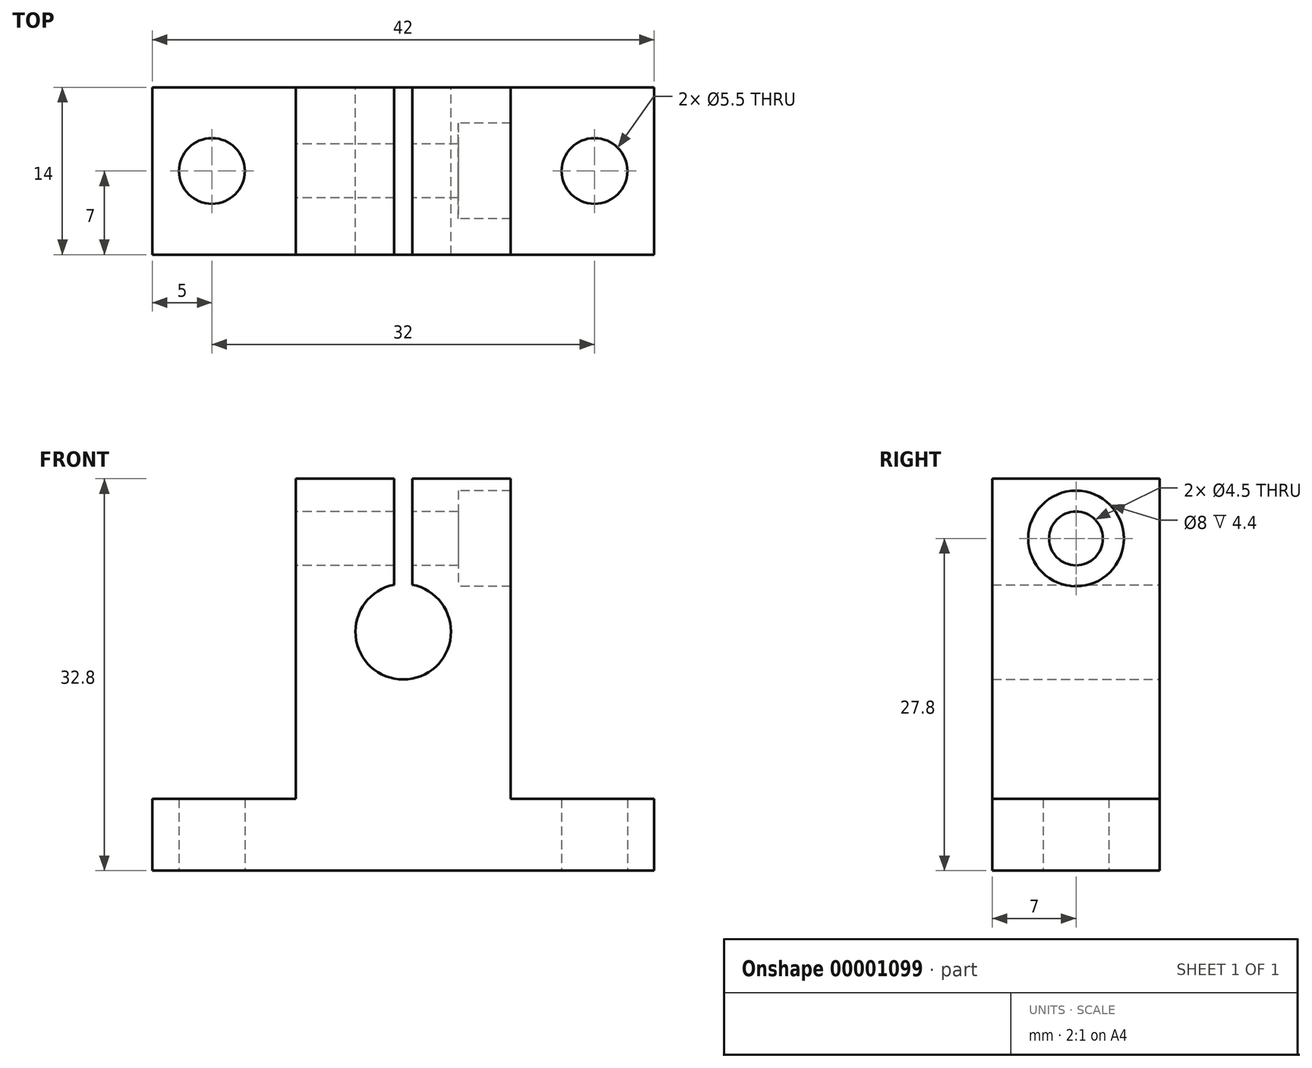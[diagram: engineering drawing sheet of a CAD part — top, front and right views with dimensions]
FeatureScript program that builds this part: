
annotation { "Feature Type Name" : "Feature", "Feature Type Description" : "" }
export const myFeature = defineFeature(function(context is Context, id is Id, definition is map)
    precondition{}
    {
        {
            var Q0;
            Q0=qCreatedBy(makeId("Front.planeOp"),FACE);
            var sketch = newSketch(context, id + "F0", { "sketchPlane" : qUnion([Q0])});
            skLineSegment(sketch, "E0", {"start": v(-21, 6) * mm, "end": v(-9, 6) * mm});
            skLineSegment(sketch, "E1", {"start": v(-9, 6) * mm, "end": v(-9, 32.8) * mm});
            skLineSegment(sketch, "E2", {"start": v(-9, 32.8) * mm, "end": v(-0.75, 32.8) * mm});
            skArc(sketch, "E3", {"start": v(-0.75, 23.93) * mm, "mid": v(0, 16) * mm, "end": v(0.75, 23.93) * mm});
            skLineSegment(sketch, "E4", {"start": v(0, 16) * mm, "end": v(0, 0) * mm, "construction": true});
            skLineSegment(sketch, "E5", {"start": v(21, 0) * mm, "end": v(-21, 0) * mm});
            skLineSegment(sketch, "E6", {"start": v(-21, 0) * mm, "end": v(-21, 6) * mm});
            skLineSegment(sketch, "E7", {"start": v(-0.75, 23.93) * mm, "end": v(-0.75, 32.8) * mm});
            skLineSegment(sketch, "E8.MirrorCS", {"start": v(21, 0) * mm, "end": v(21, 6) * mm});
            skLineSegment(sketch, "E9.MirrorCS", {"start": v(21, 6) * mm, "end": v(9, 6) * mm});
            skLineSegment(sketch, "E10.MirrorCS", {"start": v(9, 6) * mm, "end": v(9, 32.8) * mm});
            skLineSegment(sketch, "E11.MirrorCS", {"start": v(9, 32.8) * mm, "end": v(0.75, 32.8) * mm});
            skLineSegment(sketch, "E12.MirrorCS", {"start": v(0.75, 23.93) * mm, "end": v(0.75, 32.8) * mm});
            skSolve(sketch);
        }
        {
            var Q0;
            Q0=makeQuery(id+"F0.imprint","IMPRINT",FACE,{"disambiguationData":[TD([[makeQuery(id+"F0.imprint","IMPRINT",EDGE,{"derivedFrom":sQuery(id+"F0.wireOp",EDGE,"E0")}),-1.0]])]});
            extrude(context, id + "F1", {"entities" : qUnion([Q0]), "depth" : 14 * mm, "symmetric" : true});
        }
        {
            var Q0;
            Q0=makeQuery(id+"F1.opExtrude","SWEPT_FACE",FACE,{"disambiguationData":[OSD([sQuery(id+"F0.wireOp",EDGE,"E0")])]});
            var sketch = newSketch(context, id + "F2", { "sketchPlane" : qUnion([Q0])});
            skLineSegment(sketch, "E13.bottom", {"start": v(-16, 7) * mm, "end": v(16, 7) * mm, "construction": true});
            skLineSegment(sketch, "E13.top", {"start": v(-16, -7) * mm, "end": v(16, -7) * mm, "construction": true});
            skLineSegment(sketch, "E13.left", {"start": v(-16, 7) * mm, "end": v(-16, -7) * mm, "construction": true});
            skLineSegment(sketch, "E13.right", {"start": v(16, 7) * mm, "end": v(16, -7) * mm, "construction": true});
            skLineSegment(sketch, "E14", {"start": v(-16, 0) * mm, "end": v(16, 0) * mm, "construction": true});
            skSolve(sketch);
        }
        {
            var Q0;
            Q0=sQuery(id+"F2.wireOp",VERTEX,"E14.start");
            var Q1;
            Q1=sQuery(id+"F2.wireOp",VERTEX,"E14.end");
            var Q2;
            Q2=makeQuery(id+"F1.opExtrude","SWEPT_BODY",BODY,{"disambiguationData":[OSD([sQuery(id+"F0.wireOp",EDGE,"E0"),sQuery(id+"F0.wireOp",EDGE,"E1"),sQuery(id+"F0.wireOp",EDGE,"E2"),sQuery(id+"F0.wireOp",EDGE,"E3"),sQuery(id+"F0.wireOp",EDGE,"E5"),sQuery(id+"F0.wireOp",EDGE,"E6"),sQuery(id+"F0.wireOp",EDGE,"E7"),sQuery(id+"F0.wireOp",EDGE,"E8.MirrorCS"),sQuery(id+"F0.wireOp",EDGE,"E9.MirrorCS"),sQuery(id+"F0.wireOp",EDGE,"E10.MirrorCS"),sQuery(id+"F0.wireOp",EDGE,"E11.MirrorCS"),sQuery(id+"F0.wireOp",EDGE,"E12.MirrorCS")])]});
            hole(context, id + "F3", {"style" : HoleStyle.SIMPLE, "endStyle" : HoleEndStyle.THROUGH, "holeDiameter" : 5.5 * mm, "locations" : qUnion([Q0, Q1]), "scope" : qUnion([Q2]), "isTappedThrough" : true});
        }
        {
            var Q0;
            Q0=makeQuery(id+"F1.opExtrude","SWEPT_FACE",FACE,{"disambiguationData":[OSD([sQuery(id+"F0.wireOp",EDGE,"E10.MirrorCS")])]});
            var sketch = newSketch(context, id + "F4", { "sketchPlane" : qUnion([Q0])});
            skLineSegment(sketch, "E15", {"start": v(7, 27.8) * mm, "end": v(-7, 27.8) * mm, "construction": true});
            skPoint(sketch, "E16", {"position": v(0, 27.8) * mm});
            skSolve(sketch);
        }
        {
            var Q0;
            Q0=sQuery(id+"F4.wireOp",VERTEX,"E16");
            var Q1;
            Q1=makeQuery(id+"F1.opExtrude","SWEPT_BODY",BODY,{"disambiguationData":[OSD([sQuery(id+"F0.wireOp",EDGE,"E0"),sQuery(id+"F0.wireOp",EDGE,"E1"),sQuery(id+"F0.wireOp",EDGE,"E2"),sQuery(id+"F0.wireOp",EDGE,"E3"),sQuery(id+"F0.wireOp",EDGE,"E5"),sQuery(id+"F0.wireOp",EDGE,"E6"),sQuery(id+"F0.wireOp",EDGE,"E7"),sQuery(id+"F0.wireOp",EDGE,"E8.MirrorCS"),sQuery(id+"F0.wireOp",EDGE,"E9.MirrorCS"),sQuery(id+"F0.wireOp",EDGE,"E10.MirrorCS"),sQuery(id+"F0.wireOp",EDGE,"E11.MirrorCS"),sQuery(id+"F0.wireOp",EDGE,"E12.MirrorCS")])]});
            hole(context, id + "F5", {"style" : HoleStyle.C_BORE, "endStyle" : HoleEndStyle.THROUGH, "holeDiameter" : 4.5 * mm, "cBoreDiameter" : 8 * mm, "cBoreDepth" : 4.4 * mm, "locations" : qUnion([Q0]), "scope" : qUnion([Q1]), "isTappedThrough" : true});
        }
    });
